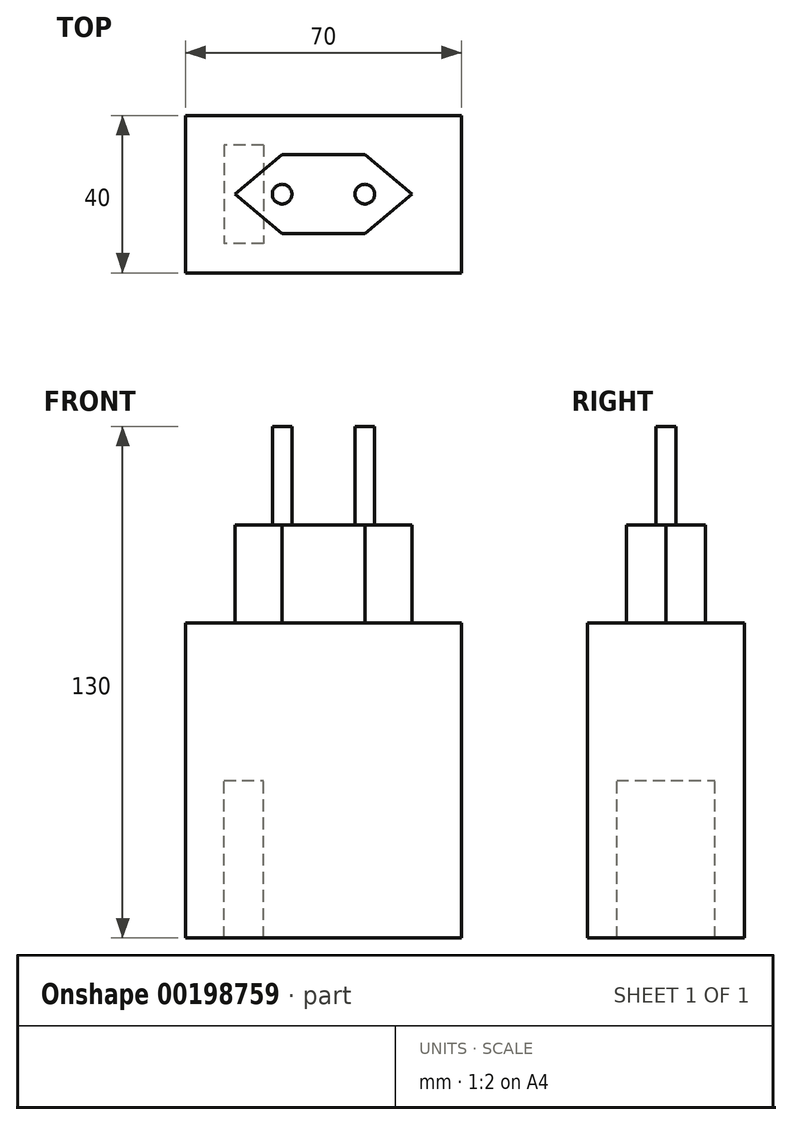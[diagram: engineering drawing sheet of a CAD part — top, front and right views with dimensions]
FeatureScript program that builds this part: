
annotation { "Feature Type Name" : "Feature", "Feature Type Description" : "" }
export const myFeature = defineFeature(function(context is Context, id is Id, definition is map)
    precondition{}
    {
        {
            var Q0;
            Q0=qCreatedBy(makeId("Front.planeOp"),FACE);
            var sketch = newSketch(context, id + "F0", { "sketchPlane" : qUnion([Q0])});
            skLineSegment(sketch, "E0.bottom", {"start": v(35, 40) * mm, "end": v(-35, 40) * mm});
            skLineSegment(sketch, "E0.top", {"start": v(35, -40) * mm, "end": v(-35, -40) * mm});
            skLineSegment(sketch, "E0.left", {"start": v(35, 40) * mm, "end": v(35, -40) * mm});
            skLineSegment(sketch, "E0.right", {"start": v(-35, 40) * mm, "end": v(-35, -40) * mm});
            skPoint(sketch, "E0.middle", {"position": v(0, 0) * mm});
            skSolve(sketch);
        }
        {
            var Q0;
            Q0 = qSketchRegion(id + "F0", true);
            extrude(context, id + "F1", {"entities" : qUnion([Q0]), "endBound" : BoundingType.SYMMETRIC, "depth" : 40 * mm});
        }
        {
            var Q0;
            Q0=makeQuery(id+"F1.opExtrude","SWEPT_FACE",FACE,{"disambiguationData":[OSD([sQuery(id+"F0.wireOp",EDGE,"E0.bottom")])]});
            var sketch = newSketch(context, id + "F2", { "sketchPlane" : qUnion([Q0])});
            skLineSegment(sketch, "E1.bottom", {"start": v(10.5, 10) * mm, "end": v(-10.5, 10) * mm});
            skLineSegment(sketch, "E1.top", {"start": v(10.5, -10) * mm, "end": v(-10.5, -10) * mm});
            skPoint(sketch, "E1.middle", {"position": v(0, 0) * mm});
            skLineSegment(sketch, "E2", {"start": v(22.5, 0) * mm, "end": v(10.5, -10) * mm});
            skLineSegment(sketch, "E3", {"start": v(22.5, 0) * mm, "end": v(10.5, 10) * mm});
            skLineSegment(sketch, "E4.MirrorCS", {"start": v(-22.5, 0) * mm, "end": v(-10.5, 10) * mm});
            skLineSegment(sketch, "E5.MirrorCS", {"start": v(-22.5, 0) * mm, "end": v(-10.5, -10) * mm});
            skPoint(sketch, "E6.orphan", {"position": v(-22.5, -10) * mm});
            skPoint(sketch, "E7.orphan", {"position": v(-22.5, 10) * mm});
            skPoint(sketch, "E8.orphan", {"position": v(22.5, 10) * mm});
            skPoint(sketch, "E9.orphan", {"position": v(22.5, -10) * mm});
            skSolve(sketch);
        }
        {
            var Q0;
            Q0 = qSketchRegion(id + "F2", true);
            extrude(context, id + "F3", {"entities" : qUnion([Q0]), "operationType" : NewBodyOperationType.ADD, "depth" : 25 * mm});
        }
        {
            var Q0;
            Q0=makeQuery(id+"F3.opExtrude","CAP_FACE",FACE,{"disambiguationData":[OSD([sQuery(id+"F2.wireOp",EDGE,"E1.bottom"),sQuery(id+"F2.wireOp",EDGE,"E1.top"),sQuery(id+"F2.wireOp",EDGE,"E2"),sQuery(id+"F2.wireOp",EDGE,"E3"),sQuery(id+"F2.wireOp",EDGE,"E4.MirrorCS"),sQuery(id+"F2.wireOp",EDGE,"E5.MirrorCS")])],"isStart":false});
            var sketch = newSketch(context, id + "F4", { "sketchPlane" : qUnion([Q0])});
            skCircle(sketch, "E10", {"center": v(-10.5, 0) * mm, "radius": 2.5 * mm});
            skCircle(sketch, "E11", {"center": v(10.5, 0) * mm, "radius": 2.5 * mm});
            skSolve(sketch);
        }
        {
            var Q0;
            Q0 = qSketchRegion(id + "F4", true);
            extrude(context, id + "F5", {"entities" : qUnion([Q0]), "operationType" : NewBodyOperationType.ADD, "depth" : 25 * mm});
        }
        {
            var Q0;
            Q0=qCreatedBy(makeId("Top.planeOp"),FACE);
            var sketch = newSketch(context, id + "F6", { "sketchPlane" : qUnion([Q0])});
            skLineSegment(sketch, "E12.bottom", {"start": v(-25.26, -12.5) * mm, "end": v(-15.26, -12.5) * mm});
            skLineSegment(sketch, "E12.top", {"start": v(-25.26, 12.5) * mm, "end": v(-15.26, 12.5) * mm});
            skLineSegment(sketch, "E12.left", {"start": v(-25.26, -12.5) * mm, "end": v(-25.26, 12.5) * mm});
            skLineSegment(sketch, "E12.right", {"start": v(-15.26, -12.5) * mm, "end": v(-15.26, 12.5) * mm});
            skPoint(sketch, "E12.middle", {"position": v(-20.26, 0) * mm});
            skSolve(sketch);
        }
        {
            var Q0;
            Q0 = qSketchRegion(id + "F6", true);
            extrude(context, id + "F7", {"entities" : qUnion([Q0]), "operationType" : NewBodyOperationType.REMOVE, "oppositeDirection" : true, "depth" : 79.4 * mm});
        }
    });
